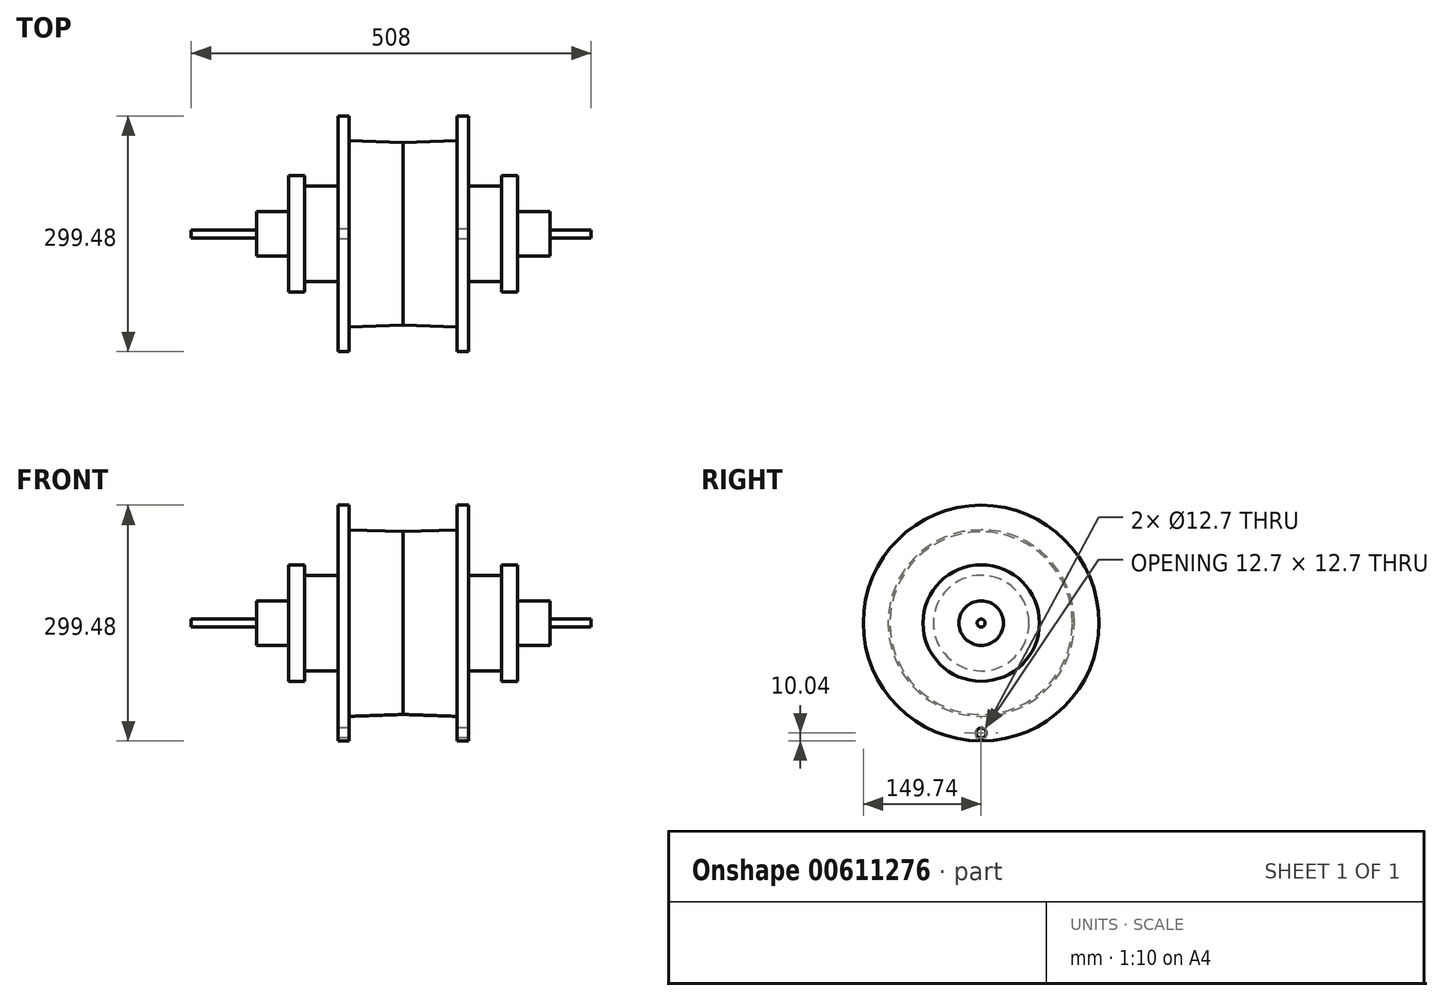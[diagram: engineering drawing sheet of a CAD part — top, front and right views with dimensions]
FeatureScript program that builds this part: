
annotation { "Feature Type Name" : "Feature", "Feature Type Description" : "" }
export const myFeature = defineFeature(function(context is Context, id is Id, definition is map)
    precondition{}
    {
        {
            var Q0;
            Q0=qCreatedBy(makeId("Right.planeOp"),FACE);
            var sketch = newSketch(context, id + "F0", { "sketchPlane" : qUnion([Q0])});
            skLineSegment(sketch, "E0", {"start": v(0, 0) * mm, "end": v(92.19, 0) * mm, "construction": true});
            skLineSegment(sketch, "E1", {"start": v(0, 0) * mm, "end": v(0, 51.06) * mm, "construction": true});
            skCircle(sketch, "E2", {"center": v(0, 0) * mm, "radius": 5.09 * mm});
            skSolve(sketch);
        }
        {
            var Q0;
            Q0 = qSketchRegion(id + "F0", true);
            extrude(context, id + "F1", {"entities" : qUnion([Q0]), "depth" : 508 * mm, "offsetDistance" : 25.4 * mm});
        }
        {
            var Q0;
            Q0=qCreatedBy(makeId("Front.planeOp"),FACE);
            var sketch = newSketch(context, id + "F2", { "sketchPlane" : qUnion([Q0])});
            skLineSegment(sketch, "E3", {"start": v(0, 0) * mm, "end": v(269.12, 0) * mm, "construction": true});
            skLineSegment(sketch, "E4", {"start": v(269.12, 0) * mm, "end": v(269.12, 116.07) * mm, "construction": true});
            skLineSegment(sketch, "E5", {"start": v(82.7, 0) * mm, "end": v(82.7, 28.26) * mm});
            skLineSegment(sketch, "E6", {"start": v(82.7, 28.26) * mm, "end": v(123.59, 28.26) * mm});
            skLineSegment(sketch, "E7", {"start": v(123.59, 28.26) * mm, "end": v(123.59, 73.97) * mm});
            skLineSegment(sketch, "E8", {"start": v(123.59, 73.97) * mm, "end": v(144.03, 73.97) * mm});
            skLineSegment(sketch, "E9", {"start": v(144.03, 73.97) * mm, "end": v(144.03, 60.74) * mm});
            skLineSegment(sketch, "E10", {"start": v(144.03, 60.74) * mm, "end": v(186.13, 60.74) * mm});
            skLineSegment(sketch, "E11", {"start": v(186.13, 60.74) * mm, "end": v(186.13, 149.74) * mm});
            skLineSegment(sketch, "E12", {"start": v(186.13, 149.74) * mm, "end": v(200.56, 149.74) * mm});
            skLineSegment(sketch, "E13", {"start": v(200.56, 149.74) * mm, "end": v(200.56, 118.47) * mm});
            skLineSegment(sketch, "E14", {"start": v(200.56, 118.47) * mm, "end": v(269.12, 116.07) * mm});
            skLineSegment(sketch, "E15.MirrorCS", {"start": v(337.68, 118.47) * mm, "end": v(269.12, 116.07) * mm});
            skLineSegment(sketch, "E16.MirrorCS", {"start": v(337.68, 149.74) * mm, "end": v(337.68, 118.47) * mm});
            skLineSegment(sketch, "E17.MirrorCS", {"start": v(352.11, 149.74) * mm, "end": v(337.68, 149.74) * mm});
            skLineSegment(sketch, "E18.MirrorCS", {"start": v(352.11, 60.74) * mm, "end": v(352.11, 149.74) * mm});
            skLineSegment(sketch, "E19.MirrorCS", {"start": v(394.2, 60.74) * mm, "end": v(352.11, 60.74) * mm});
            skLineSegment(sketch, "E20.MirrorCS", {"start": v(414.66, 73.97) * mm, "end": v(394.2, 73.97) * mm});
            skLineSegment(sketch, "E21.MirrorCS", {"start": v(414.66, 28.26) * mm, "end": v(414.66, 73.97) * mm});
            skLineSegment(sketch, "E22.MirrorCS", {"start": v(394.2, 73.97) * mm, "end": v(394.2, 60.74) * mm});
            skLineSegment(sketch, "E23.MirrorCS", {"start": v(455.55, 28.26) * mm, "end": v(414.66, 28.26) * mm});
            skLineSegment(sketch, "E24.MirrorCS", {"start": v(455.55, 0) * mm, "end": v(455.55, 28.26) * mm});
            skLineSegment(sketch, "E25", {"start": v(82.7, 0) * mm, "end": v(455.55, 0) * mm});
            skSolve(sketch);
        }
        {
            var Q0;
            Q0 = qSketchRegion(id + "F2", true);
            var Q1;
            Q1=sQuery(id+"F2.wireOp",EDGE,"E25");
            revolve(context, id + "F3", {"operationType" : NewBodyOperationType.ADD, "entities" : qUnion([Q0]), "axis" : qUnion([Q1]), "revolveType" : RevolveType.FULL, "oppositeDirection" : true});
        }
        {
            var Q0;
            Q0=qCreatedBy(makeId("Right.planeOp"),FACE);
            var sketch = newSketch(context, id + "F4", { "sketchPlane" : qUnion([Q0])});
            skCircle(sketch, "E26", {"center": v(0, 139.7) * mm, "radius": 6.35 * mm});
            skLineSegment(sketch, "E27", {"start": v(0, 139.7) * mm, "end": v(0, 0) * mm, "construction": true});
            skLineSegment(sketch, "E28", {"start": v(0, 0) * mm, "end": v(-185.36, 0) * mm, "construction": true});
            skLineSegment(sketch, "E29.MirrorCS", {"start": v(0, -139.7) * mm, "end": v(0, 0) * mm, "construction": true});
            skCircle(sketch, "E30", {"center": v(0, -139.7) * mm, "radius": 6.35 * mm});
            skSolve(sketch);
        }
        {
            var Q0;
            Q0=makeQuery(id+"F4.imprint","IMPRINT",FACE,{"disambiguationData":[TD([[makeQuery(id+"F4.imprint","IMPRINT",EDGE,{"derivedFrom":sQuery(id+"F4.wireOp",EDGE,"E26")}),-1.0]])]});
            var Q1;
            Q1=makeQuery(id+"F4.imprint","IMPRINT",FACE,{"disambiguationData":[TD([[makeQuery(id+"F4.imprint","IMPRINT",EDGE,{"derivedFrom":sQuery(id+"F4.wireOp",EDGE,"E30")}),1.0]])]});
            extrude(context, id + "F5", {"entities" : qUnion([Q0, Q1]), "operationType" : NewBodyOperationType.REMOVE, "endBound" : BoundingType.THROUGH_ALL, "depth" : 119.38 * mm, "offsetDistance" : 25.4 * mm});
        }
    });
